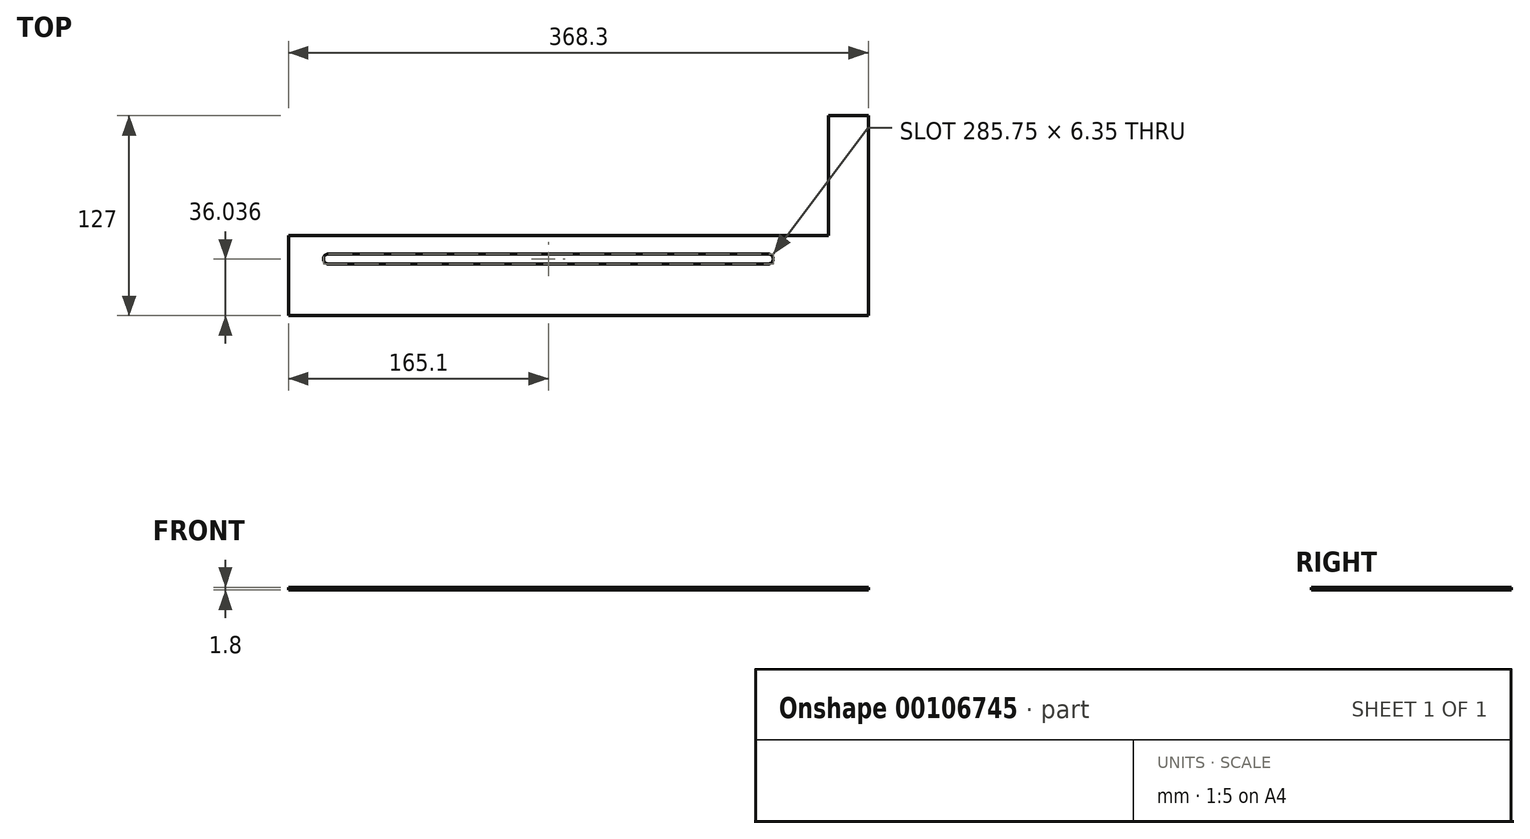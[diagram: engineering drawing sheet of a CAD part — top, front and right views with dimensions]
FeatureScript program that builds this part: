
annotation { "Feature Type Name" : "Feature", "Feature Type Description" : "" }
export const myFeature = defineFeature(function(context is Context, id is Id, definition is map)
    precondition{}
    {
        {
            var Q0;
            Q0=qCreatedBy(makeId("Right.planeOp"),FACE);
            var sketch = newSketch(context, id + "F0", { "sketchPlane" : qUnion([Q0])});
            skLineSegment(sketch, "E0.bottom", {"start": v(25.4, 0.9) * mm, "end": v(-25.4, 0.9) * mm});
            skLineSegment(sketch, "E0.top", {"start": v(25.4, -0.9) * mm, "end": v(-25.4, -0.9) * mm});
            skLineSegment(sketch, "E0.left", {"start": v(25.4, 0.9) * mm, "end": v(25.4, -0.9) * mm});
            skLineSegment(sketch, "E0.right", {"start": v(-25.4, 0.9) * mm, "end": v(-25.4, -0.9) * mm});
            skPoint(sketch, "E0.middle", {"position": v(0, 0) * mm});
            skSolve(sketch);
        }
        {
            var Q0;
            Q0 = qSketchRegion(id + "F0", true);
            extrude(context, id + "F1", {"entities" : qUnion([Q0]), "depth" : 171.45 * mm, "hasSecondDirection" : true, "secondDirectionOppositeDirection" : true, "secondDirectionDepth" : 171.45 * mm});
        }
        {
            var Q0;
            Q0=makeQuery(id+"F1.opExtrude","SWEPT_FACE",FACE,{"disambiguationData":[OSD([sQuery(id+"F0.wireOp",EDGE,"E0.bottom")])]});
            var sketch = newSketch(context, id + "F2", { "sketchPlane" : qUnion([Q0])});
            skLineSegment(sketch, "E1", {"start": v(0, 0) * mm, "end": v(0, -25.4) * mm, "construction": true});
            skLineSegment(sketch, "E2", {"start": v(0, -25.4) * mm, "end": v(171.45, -25.4) * mm, "construction": true});
            skLineSegment(sketch, "E3", {"start": v(171.45, -25.4) * mm, "end": v(171.45, 101.6) * mm});
            skLineSegment(sketch, "E4", {"start": v(171.45, 101.6) * mm, "end": v(196.85, 101.6) * mm});
            skLineSegment(sketch, "E5", {"start": v(196.85, 101.6) * mm, "end": v(196.85, -25.4) * mm});
            skLineSegment(sketch, "E6", {"start": v(171.45, -25.4) * mm, "end": v(196.85, -25.4) * mm});
            skSolve(sketch);
        }
        {
            var Q0;
            Q0 = qSketchRegion(id + "F2", true);
            extrude(context, id + "F3", {"entities" : qUnion([Q0]), "operationType" : NewBodyOperationType.ADD, "oppositeDirection" : true, "depth" : 1.8 * mm});
        }
        {
            var Q0;
            Q0=makeQuery(id+"F3.boolean.opBoolean","MERGE",FACE,{"derivedFrom":[makeQuery(id+"F1.opExtrude","SWEPT_FACE",FACE,{"disambiguationData":[OSD([sQuery(id+"F0.wireOp",EDGE,"E0.bottom")])]}),makeQuery(id+"F3.opExtrude","CAP_FACE",FACE,{"disambiguationData":[OSD([sQuery(id+"F2.wireOp",EDGE,"E3"),sQuery(id+"F2.wireOp",EDGE,"E4"),sQuery(id+"F2.wireOp",EDGE,"E5"),sQuery(id+"F2.wireOp",EDGE,"E6")])],"isStart":true})]});
            var sketch = newSketch(context, id + "F4", { "sketchPlane" : qUnion([Q0])});
            skLineSegment(sketch, "E7", {"start": v(-146.05, 10.64) * mm, "end": v(133.35, 10.64) * mm, "construction": true});
            skArc(sketch, "E8.0.startCap", {"start": v(-146.05, 7.46) * mm, "mid": v(-149.23, 10.64) * mm, "end": v(-146.05, 13.81) * mm});
            skArc(sketch, "E8.0.endCap", {"start": v(133.35, 13.81) * mm, "mid": v(136.53, 10.64) * mm, "end": v(133.35, 7.46) * mm});
            skLineSegment(sketch, "E8.0.left", {"start": v(-146.05, 13.81) * mm, "end": v(133.35, 13.81) * mm});
            skLineSegment(sketch, "E8.0.right", {"start": v(-146.05, 7.46) * mm, "end": v(133.35, 7.46) * mm});
            skSolve(sketch);
        }
        {
            var Q0;
            Q0 = qSketchRegion(id + "F4", true);
            extrude(context, id + "F5", {"entities" : qUnion([Q0]), "operationType" : NewBodyOperationType.REMOVE, "endBound" : BoundingType.THROUGH_ALL, "oppositeDirection" : true, "depth" : 25.4 * mm});
        }
    });
